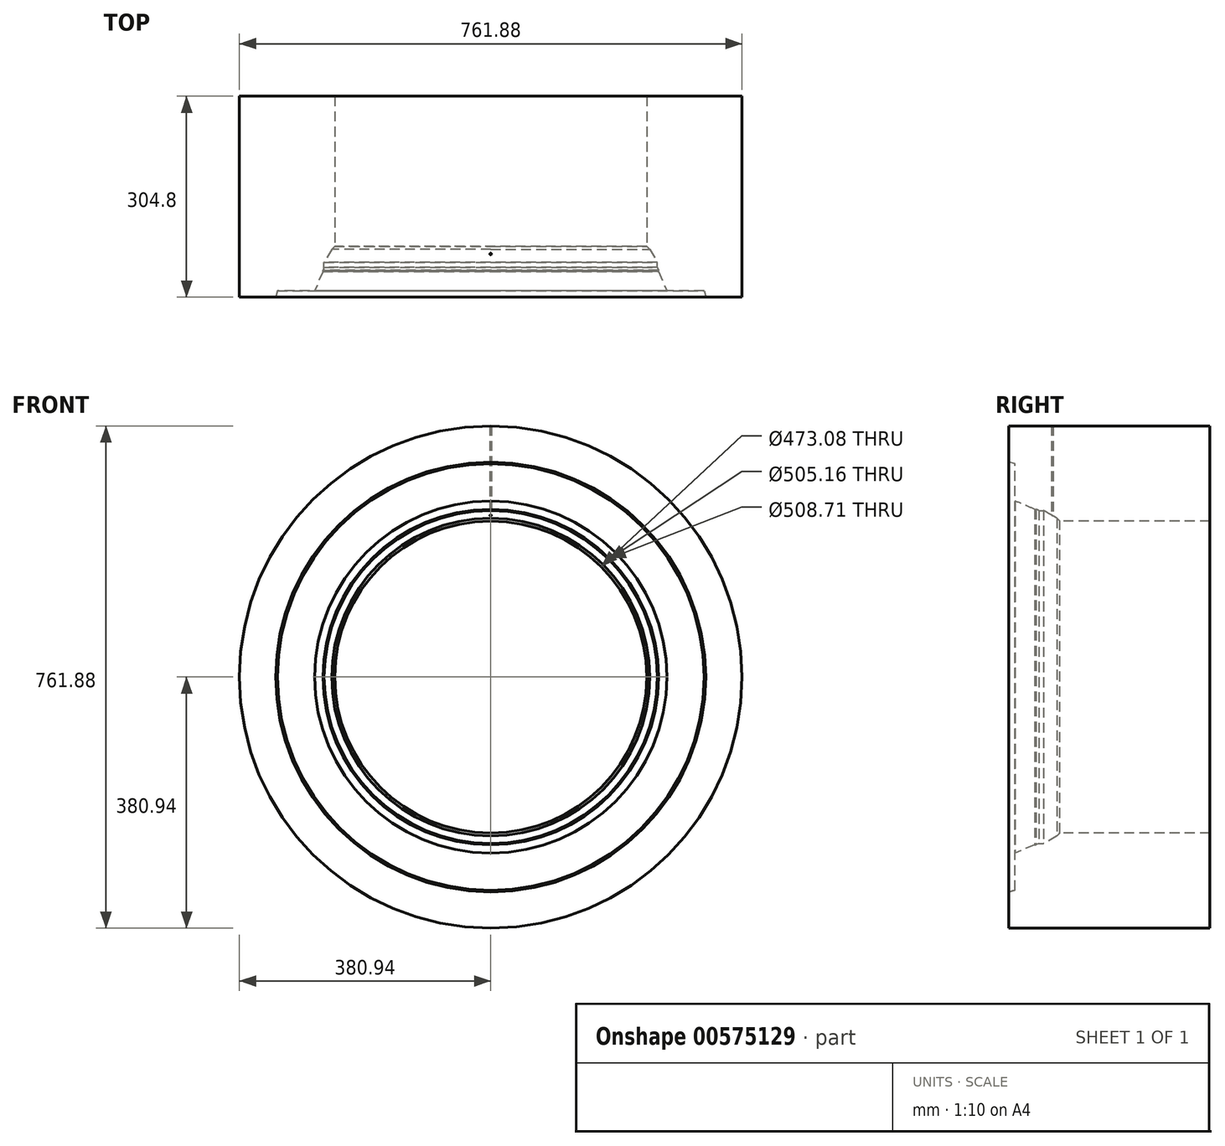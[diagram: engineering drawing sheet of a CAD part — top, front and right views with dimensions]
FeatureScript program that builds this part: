
annotation { "Feature Type Name" : "Feature", "Feature Type Description" : "" }
export const myFeature = defineFeature(function(context is Context, id is Id, definition is map)
    precondition{}
    {
        {
            var Q0;
            Q0=qCreatedBy(makeId("Front.planeOp"),FACE);
            var sketch = newSketch(context, id + "F0", { "sketchPlane" : qUnion([Q0])});
            skCircle(sketch, "E0", {"center": v(0, 0) * mm, "radius": 236.54 * mm});
            skCircle(sketch, "E1", {"center": v(0, 0) * mm, "radius": 380.94 * mm});
            skSolve(sketch);
        }
        {
            var Q0;
            Q0 = qSketchRegion(id + "F0", true);
            extrude(context, id + "F1", {"entities" : qUnion([Q0]), "oppositeDirection" : true, "depth" : 304.8 * mm, "offsetDistance" : 25.4 * mm});
        }
        {
            var Q0;
            Q0=qCreatedBy(makeId("Right.planeOp"),FACE);
            var sketch = newSketch(context, id + "F2", { "sketchPlane" : qUnion([Q0])});
            skLineSegment(sketch, "E2", {"start": v(0, 0) * mm, "end": v(-223.81, 0) * mm});
            skPoint(sketch, "E3", {"position": v(0, 325.9) * mm});
            skLineSegment(sketch, "E4", {"start": v(9.52, 323.44) * mm, "end": v(9.53, 0) * mm});
            skLineSegment(sketch, "E5", {"start": v(0, 325.9) * mm, "end": v(9.53, 323.44) * mm});
            skLineSegment(sketch, "E6", {"start": v(0, 0) * mm, "end": v(9.53, 0) * mm});
            skLineSegment(sketch, "E7", {"start": v(0, 325.9) * mm, "end": v(-38.14, 325.9) * mm});
            skLineSegment(sketch, "E8", {"start": v(-38.14, 325.9) * mm, "end": v(0, -5.87) * mm});
            skSolve(sketch);
        }
        {
            var Q0;
            Q0 = qSketchRegion(id + "F2", true);
            var Q1;
            Q1=sQuery(id+"F2.wireOp",EDGE,"E2");
            revolve(context, id + "F3", {"operationType" : NewBodyOperationType.REMOVE, "entities" : qUnion([Q0]), "axis" : qUnion([Q1]), "revolveType" : RevolveType.FULL, "oppositeDirection" : true});
        }
        {
            var Q0;
            Q0=qCreatedBy(makeId("Right.planeOp"),FACE);
            var sketch = newSketch(context, id + "F4", { "sketchPlane" : qUnion([Q0])});
            skPoint(sketch, "E9", {"position": v(9.52, 267) * mm});
            skLineSegment(sketch, "E10", {"start": v(9.52, 267) * mm, "end": v(39.3, 254.36) * mm});
            skLineSegment(sketch, "E11", {"start": v(41.25, 254.36) * mm, "end": v(39.3, 254.36) * mm});
            skLineSegment(sketch, "E12", {"start": v(41.25, 254.36) * mm, "end": v(45.44, 252.58) * mm});
            skLineSegment(sketch, "E13", {"start": v(45.44, 252.58) * mm, "end": v(52.7, 252.58) * mm});
            skLineSegment(sketch, "E14", {"start": v(52.7, 252.58) * mm, "end": v(72.8, 240.98) * mm});
            skLineSegment(sketch, "E15", {"start": v(72.8, 240.98) * mm, "end": v(83.79, 229.98) * mm});
            skLineSegment(sketch, "E16", {"start": v(9.52, 267) * mm, "end": v(-83.95, 267) * mm});
            skLineSegment(sketch, "E17", {"start": v(-83.95, 267) * mm, "end": v(-48.08, 188) * mm});
            skLineSegment(sketch, "E18", {"start": v(-48.08, 188) * mm, "end": v(83.79, 229.98) * mm});
            skSolve(sketch);
        }
        {
            var Q0;
            Q0 = qSketchRegion(id + "F4", true);
            var Q1;
            Q1=makeQuery(id+"F1.opExtrude","SWEPT_FACE",FACE,{"disambiguationData":[OSD([sQuery(id+"F0.wireOp",EDGE,"E0")])]});
            revolve(context, id + "F5", {"operationType" : NewBodyOperationType.REMOVE, "entities" : qUnion([Q0]), "axis" : qUnion([Q1]), "revolveType" : RevolveType.FULL, "oppositeDirection" : true});
        }
        {
            var Q0;
            Q0=qCreatedBy(makeId("Top.planeOp"),FACE);
            var sketch = newSketch(context, id + "F6", { "sketchPlane" : qUnion([Q0])});
            skCircle(sketch, "E19", {"center": v(0, 65.6) * mm, "radius": 1.27 * mm});
            skSolve(sketch);
        }
        {
            var Q0;
            Q0 = qSketchRegion(id + "F6", true);
            extrude(context, id + "F7", {"entities" : qUnion([Q0]), "operationType" : NewBodyOperationType.REMOVE, "endBound" : BoundingType.THROUGH_ALL, "depth" : 214.38 * mm, "offsetDistance" : 25.4 * mm});
        }
    });
